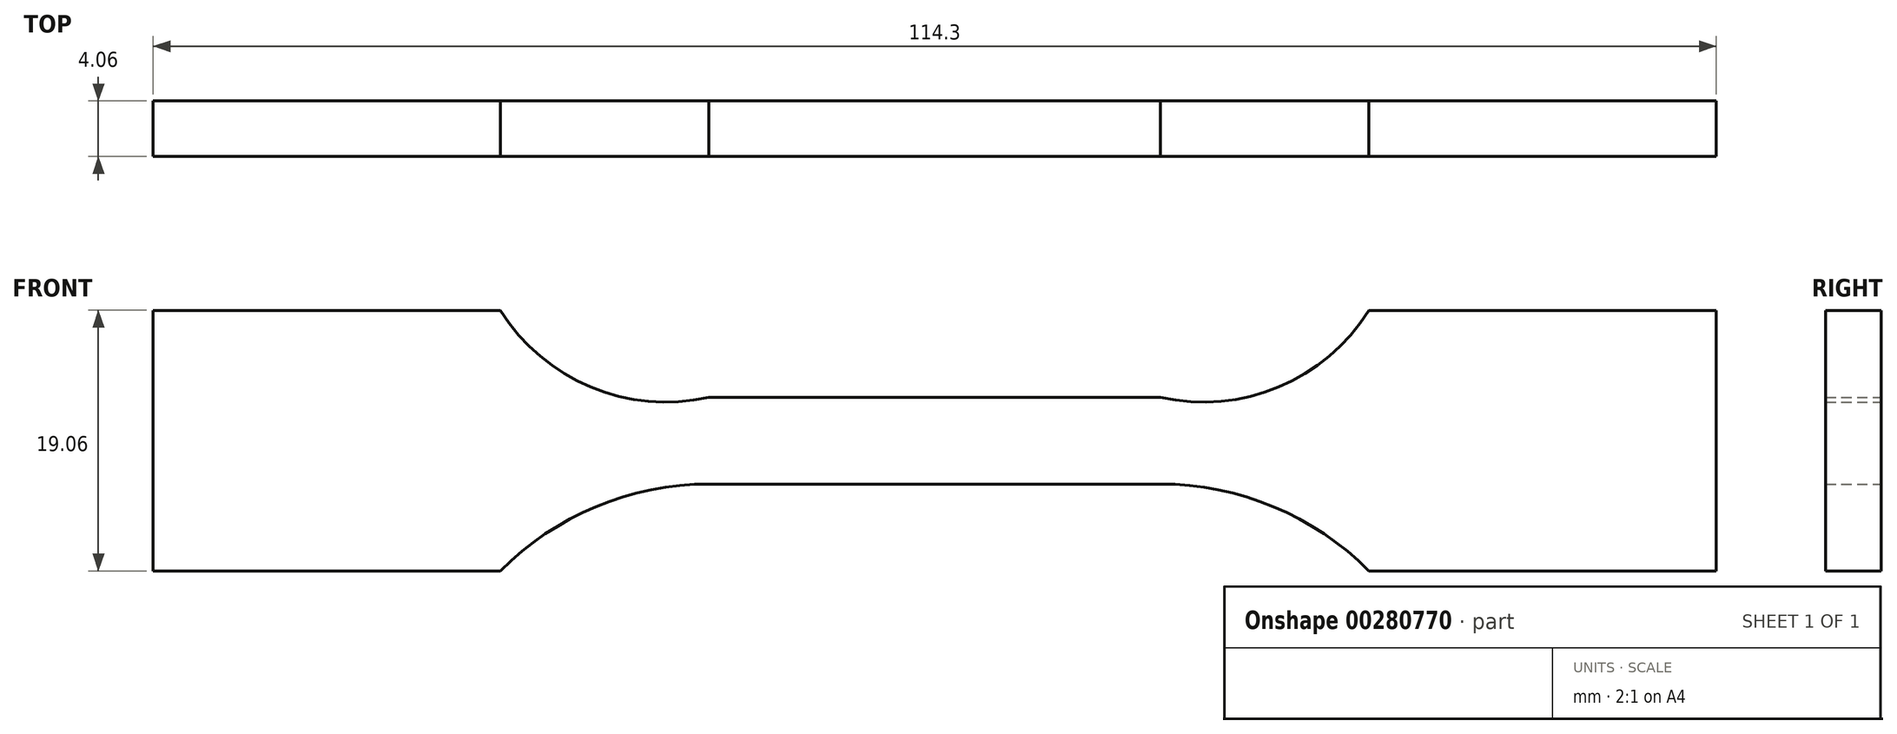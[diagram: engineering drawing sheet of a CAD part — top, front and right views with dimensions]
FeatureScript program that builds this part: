
annotation { "Feature Type Name" : "Feature", "Feature Type Description" : "" }
export const myFeature = defineFeature(function(context is Context, id is Id, definition is map)
    precondition{}
    {
        {
            var Q0;
            Q0=qCreatedBy(makeId("Front.planeOp"),FACE);
            var sketch = newSketch(context, id + "F0", { "sketchPlane" : qUnion([Q0])});
            skLineSegment(sketch, "E0", {"start": v(0, 3.18) * mm, "end": v(16.51, 3.18) * mm});
            skLineSegment(sketch, "E1", {"start": v(31.75, 9.53) * mm, "end": v(57.15, 9.53) * mm});
            skLineSegment(sketch, "E2.MirrorCS", {"start": v(0, -3.18) * mm, "end": v(16.51, -3.18) * mm});
            skLineSegment(sketch, "E3.MirrorCS", {"start": v(31.75, -9.52) * mm, "end": v(57.15, -9.52) * mm});
            skLineSegment(sketch, "E4.MirrorCS", {"start": v(-31.75, -9.52) * mm, "end": v(-57.15, -9.52) * mm});
            skLineSegment(sketch, "E5.MirrorCS", {"start": v(-31.75, 9.53) * mm, "end": v(-57.15, 9.52) * mm});
            skLineSegment(sketch, "E6.MirrorCS", {"start": v(0, -3.18) * mm, "end": v(-16.51, -3.18) * mm});
            skLineSegment(sketch, "E7.MirrorCS", {"start": v(0, 3.18) * mm, "end": v(-16.51, 3.18) * mm});
            skLineSegment(sketch, "E8", {"start": v(-57.15, 9.52) * mm, "end": v(-57.15, -9.52) * mm});
            skLineSegment(sketch, "E9", {"start": v(57.15, 9.52) * mm, "end": v(57.15, -9.52) * mm});
            skArc(sketch, "E10", {"start": v(-31.75, 9.52) * mm, "mid": v(-25.15, 3.91) * mm, "end": v(-16.51, 3.18) * mm});
            skArc(sketch, "E11", {"start": v(-16.51, -3.18) * mm, "mid": v(-24.77, -4.83) * mm, "end": v(-31.75, -9.53) * mm});
            skArc(sketch, "E12", {"start": v(16.51, 3.17) * mm, "mid": v(25.15, 3.91) * mm, "end": v(31.75, 9.53) * mm});
            skArc(sketch, "E13", {"start": v(31.75, -9.53) * mm, "mid": v(24.77, -4.83) * mm, "end": v(16.5, -3.17) * mm});
            skSolve(sketch);
        }
        {
            var Q0;
            Q0 = qSketchRegion(id + "F0", true);
            extrude(context, id + "F1", {"entities" : qUnion([Q0]), "depth" : 4.06 * mm});
        }
    });
